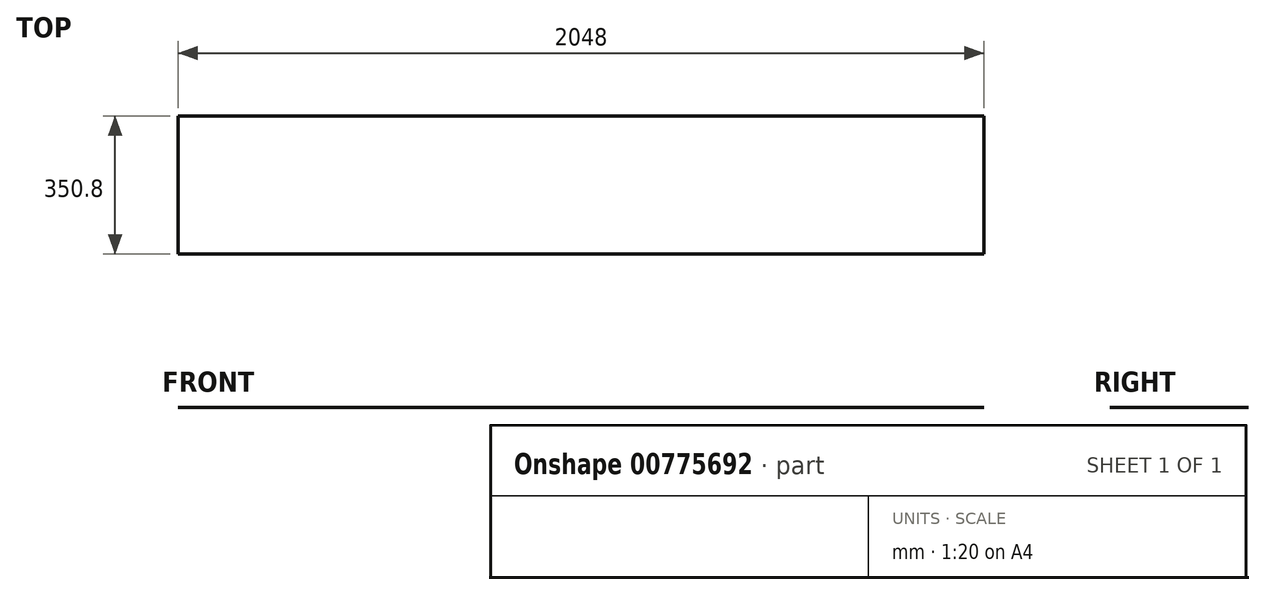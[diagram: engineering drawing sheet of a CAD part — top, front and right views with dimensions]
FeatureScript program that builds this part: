
annotation { "Feature Type Name" : "Feature", "Feature Type Description" : "" }
export const myFeature = defineFeature(function(context is Context, id is Id, definition is map)
    precondition{}
    {
        {
            var Q0;
            Q0=qCreatedBy(makeId("Top.planeOp"),FACE);
            var sketch = newSketch(context, id + "F0", { "sketchPlane" : qUnion([Q0])});
            skLineSegment(sketch, "E0.bottom", {"start": v(1024, -175.4) * mm, "end": v(-1024, -175.4) * mm});
            skLineSegment(sketch, "E0.top", {"start": v(1024, 175.4) * mm, "end": v(-1024, 175.4) * mm});
            skLineSegment(sketch, "E0.left", {"start": v(1024, -175.4) * mm, "end": v(1024, 175.4) * mm});
            skLineSegment(sketch, "E0.right", {"start": v(-1024, -175.4) * mm, "end": v(-1024, 175.4) * mm});
            skPoint(sketch, "E0.middle", {"position": v(0, 0) * mm});
            skSolve(sketch);
        }
        {
            var Q0;
            Q0=makeQuery(id+"F0.imprint","IMPRINT",FACE,{"disambiguationData":[TD([[makeQuery(id+"F0.imprint","IMPRINT",EDGE,{"derivedFrom":sQuery(id+"F0.wireOp",EDGE,"E0.bottom")}),-1.0]])]});
            extrude(context, id + "F1", {"entities" : qUnion([Q0]), "depth" : 1 / 406.4 * mm, "offsetDistance" : 25 * mm});
        }
    });
